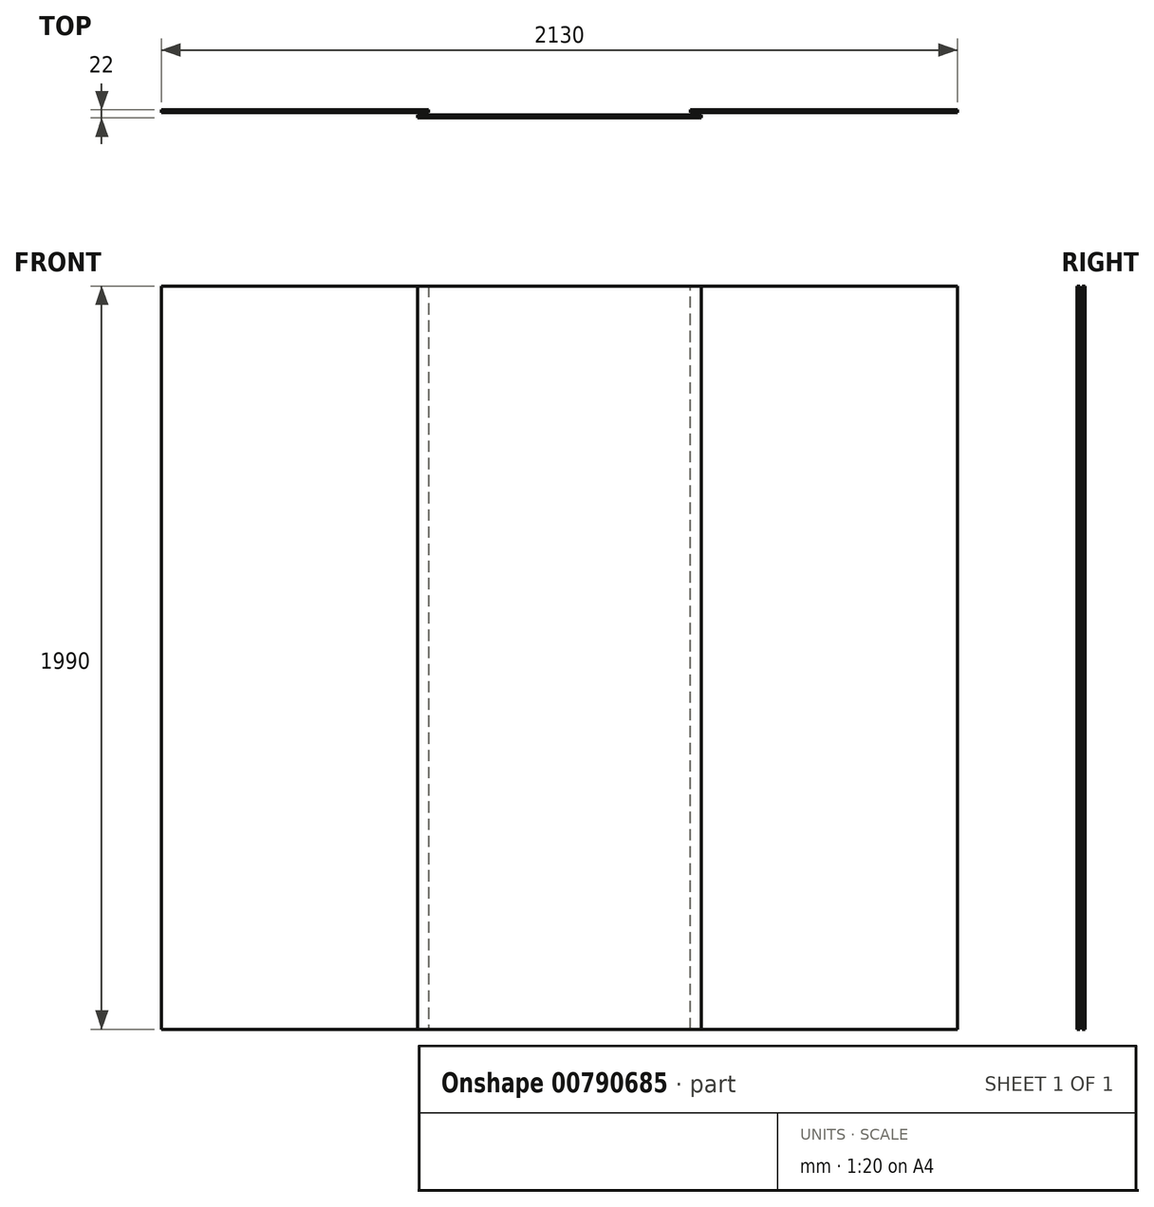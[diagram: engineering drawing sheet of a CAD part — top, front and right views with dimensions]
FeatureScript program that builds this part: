
annotation { "Feature Type Name" : "Feature", "Feature Type Description" : "" }
export const myFeature = defineFeature(function(context is Context, id is Id, definition is map)
    precondition{}
    {
        {
            var Q0;
            Q0=qCreatedBy(makeId("Front.planeOp"),FACE);
            var sketch = newSketch(context, id + "F0", { "sketchPlane" : qUnion([Q0])});
            skLineSegment(sketch, "E0.bottom", {"start": v(0, 0) * mm, "end": v(2140, 0) * mm});
            skLineSegment(sketch, "E0.top", {"start": v(0, 2000) * mm, "end": v(2140, 2000) * mm});
            skLineSegment(sketch, "E0.left", {"start": v(0, 0) * mm, "end": v(0, 2000) * mm});
            skLineSegment(sketch, "E0.right", {"start": v(2140, 0) * mm, "end": v(2140, 2000) * mm});
            skLineSegment(sketch, "E1.bottom", {"start": v(5, 1995) * mm, "end": v(2135, 1995) * mm});
            skLineSegment(sketch, "E1.top", {"start": v(5, 5) * mm, "end": v(2135, 5) * mm});
            skLineSegment(sketch, "E1.left", {"start": v(5, 1995) * mm, "end": v(5, 5) * mm});
            skLineSegment(sketch, "E1.right", {"start": v(2135, 1995) * mm, "end": v(2135, 5) * mm});
            skLineSegment(sketch, "E2.bottom", {"start": v(20, 1950) * mm, "end": v(2120, 1950) * mm});
            skLineSegment(sketch, "E2.top", {"start": v(20, 50) * mm, "end": v(2120, 50) * mm});
            skLineSegment(sketch, "E2.left", {"start": v(20, 1950) * mm, "end": v(20, 50) * mm});
            skLineSegment(sketch, "E2.right", {"start": v(2120, 1950) * mm, "end": v(2120, 50) * mm});
            skLineSegment(sketch, "E3", {"start": v(720, 1995) * mm, "end": v(720, 5) * mm});
            skLineSegment(sketch, "E4", {"start": v(1420, 5) * mm, "end": v(1420, 1995) * mm});
            skLineSegment(sketch, "E5", {"start": v(720, 1000) * mm, "end": v(5, 1000) * mm, "construction": true});
            skLineSegment(sketch, "E6", {"start": v(1420, 1000) * mm, "end": v(2135, 1000) * mm, "construction": true});
            skLineSegment(sketch, "E7", {"start": v(690, 1995) * mm, "end": v(690, 5) * mm});
            skLineSegment(sketch, "E8", {"start": v(1450, 5) * mm, "end": v(1450, 1995) * mm});
            skSolve(sketch);
        }
        {
            var Q0;
            {var subQ0=sQuery(id+"F0.wireOp",EDGE,"E2.left");Q0=makeQuery(id+"F0.imprint","IMPRINT",FACE,{"disambiguationData":[TD([[makeQuery(id+"F0.imprint","IMPRINT",EDGE,{"derivedFrom":subQ0}),1.0]])]});}
            var Q1;
            {var subQ0=sQuery(id+"F0.wireOp",EDGE,"E2.right");Q1=makeQuery(id+"F0.imprint","IMPRINT",FACE,{"disambiguationData":[TD([[makeQuery(id+"F0.imprint","IMPRINT",EDGE,{"derivedFrom":subQ0}),-1.0]])]});}
            var Q2;
            {var subQ4=sQuery(id+"F0.wireOp",EDGE,"E1.right");Q2=makeQuery(id+"F0.imprint","IMPRINT",FACE,{"disambiguationData":[TD([[makeQuery(id+"F0.imprint","IMPRINT",EDGE,{"derivedFrom":subQ4}),-1.0]])]});}
            var Q3;
            {var subQ4=sQuery(id+"F0.wireOp",EDGE,"E1.left");Q3=makeQuery(id+"F0.imprint","IMPRINT",FACE,{"disambiguationData":[TD([[makeQuery(id+"F0.imprint","IMPRINT",EDGE,{"derivedFrom":subQ4}),1.0]])]});}
            var Q4;
            {var subQ0=sQuery(id+"F0.wireOp",EDGE,"E3");var subQ1=sQuery(id+"F0.wireOp",EDGE,"E1.bottom");var subQ2=makeQuery(id+"F0.imprint","INTERSECT",VERTEX,{"derivedFrom":[subQ1,subQ0]});Q4=makeQuery(id+"F0.imprint","IMPRINT",FACE,{"disambiguationData":[TD([[makeQuery(id+"F0.imprint","IMPRINT",EDGE,{"disambiguationData":[TD([[subQ2,1.0]])],"derivedFrom":subQ1}),-1.0]])]});}
            var Q5;
            {var subQ0=sQuery(id+"F0.wireOp",EDGE,"E7");var subQ1=sQuery(id+"F0.wireOp",EDGE,"E2.bottom");var subQ2=makeQuery(id+"F0.imprint","INTERSECT",VERTEX,{"derivedFrom":[subQ1,subQ0]});Q5=makeQuery(id+"F0.imprint","IMPRINT",FACE,{"disambiguationData":[TD([[makeQuery(id+"F0.imprint","IMPRINT",EDGE,{"disambiguationData":[TD([[subQ2,-1.0]])],"derivedFrom":subQ1}),-1.0]])]});}
            var Q6;
            {var subQ0=sQuery(id+"F0.wireOp",EDGE,"E4");var subQ1=sQuery(id+"F0.wireOp",EDGE,"E1.bottom");var subQ2=makeQuery(id+"F0.imprint","INTERSECT",VERTEX,{"derivedFrom":[subQ1,subQ0]});Q6=makeQuery(id+"F0.imprint","IMPRINT",FACE,{"disambiguationData":[TD([[makeQuery(id+"F0.imprint","IMPRINT",EDGE,{"disambiguationData":[TD([[subQ2,-1.0]])],"derivedFrom":subQ1}),-1.0]])]});}
            var Q7;
            {var subQ0=sQuery(id+"F0.wireOp",EDGE,"E4");var subQ1=sQuery(id+"F0.wireOp",EDGE,"E2.bottom");var subQ2=makeQuery(id+"F0.imprint","INTERSECT",VERTEX,{"derivedFrom":[subQ1,subQ0]});Q7=makeQuery(id+"F0.imprint","IMPRINT",FACE,{"disambiguationData":[TD([[makeQuery(id+"F0.imprint","IMPRINT",EDGE,{"disambiguationData":[TD([[subQ2,-1.0]])],"derivedFrom":subQ1}),-1.0]])]});}
            var Q8;
            {var subQ0=sQuery(id+"F0.wireOp",EDGE,"E4");var subQ1=sQuery(id+"F0.wireOp",EDGE,"E1.top");var subQ2=makeQuery(id+"F0.imprint","INTERSECT",VERTEX,{"derivedFrom":[subQ1,subQ0]});Q8=makeQuery(id+"F0.imprint","IMPRINT",FACE,{"disambiguationData":[TD([[makeQuery(id+"F0.imprint","IMPRINT",EDGE,{"disambiguationData":[TD([[subQ2,-1.0]])],"derivedFrom":subQ1}),1.0]])]});}
            var Q9;
            {var subQ0=sQuery(id+"F0.wireOp",EDGE,"E3");var subQ1=sQuery(id+"F0.wireOp",EDGE,"E1.top");var subQ2=makeQuery(id+"F0.imprint","INTERSECT",VERTEX,{"derivedFrom":[subQ1,subQ0]});Q9=makeQuery(id+"F0.imprint","IMPRINT",FACE,{"disambiguationData":[TD([[makeQuery(id+"F0.imprint","IMPRINT",EDGE,{"disambiguationData":[TD([[subQ2,1.0]])],"derivedFrom":subQ1}),1.0]])]});}
            extrude(context, id + "F1", {"entities" : qUnion([Q0, Q1, Q2, Q3, Q4, Q5, Q6, Q7, Q8, Q9]), "oppositeDirection" : true, "depth" : 11 * mm, "offsetDistance" : 25 * mm, "hasSecondDirection" : true, "secondDirectionOppositeDirection" : true, "secondDirectionDepth" : 3 * mm});
        }
        {
            var Q0;
            {var subQ0=sQuery(id+"F0.wireOp",EDGE,"E3");var subQ1=sQuery(id+"F0.wireOp",EDGE,"E1.bottom");var subQ2=makeQuery(id+"F0.imprint","INTERSECT",VERTEX,{"derivedFrom":[subQ1,subQ0]});Q0=makeQuery(id+"F0.imprint","IMPRINT",FACE,{"disambiguationData":[TD([[makeQuery(id+"F0.imprint","IMPRINT",EDGE,{"disambiguationData":[TD([[subQ2,-1.0]])],"derivedFrom":subQ1}),-1.0]])]});}
            var Q1;
            {var subQ0=sQuery(id+"F0.wireOp",EDGE,"E3");var subQ1=sQuery(id+"F0.wireOp",EDGE,"E2.bottom");var subQ2=makeQuery(id+"F0.imprint","INTERSECT",VERTEX,{"derivedFrom":[subQ1,subQ0]});Q1=makeQuery(id+"F0.imprint","IMPRINT",FACE,{"disambiguationData":[TD([[makeQuery(id+"F0.imprint","IMPRINT",EDGE,{"disambiguationData":[TD([[subQ2,-1.0]])],"derivedFrom":subQ1}),-1.0]])]});}
            var Q2;
            {var subQ0=sQuery(id+"F0.wireOp",EDGE,"E4");var subQ1=sQuery(id+"F0.wireOp",EDGE,"E1.bottom");var subQ2=makeQuery(id+"F0.imprint","INTERSECT",VERTEX,{"derivedFrom":[subQ1,subQ0]});Q2=makeQuery(id+"F0.imprint","IMPRINT",FACE,{"disambiguationData":[TD([[makeQuery(id+"F0.imprint","IMPRINT",EDGE,{"disambiguationData":[TD([[subQ2,-1.0]])],"derivedFrom":subQ1}),-1.0]])]});}
            var Q3;
            {var subQ0=sQuery(id+"F0.wireOp",EDGE,"E4");var subQ1=sQuery(id+"F0.wireOp",EDGE,"E2.bottom");var subQ2=makeQuery(id+"F0.imprint","INTERSECT",VERTEX,{"derivedFrom":[subQ1,subQ0]});Q3=makeQuery(id+"F0.imprint","IMPRINT",FACE,{"disambiguationData":[TD([[makeQuery(id+"F0.imprint","IMPRINT",EDGE,{"disambiguationData":[TD([[subQ2,-1.0]])],"derivedFrom":subQ1}),-1.0]])]});}
            var Q4;
            {var subQ0=sQuery(id+"F0.wireOp",EDGE,"E3");var subQ1=sQuery(id+"F0.wireOp",EDGE,"E1.bottom");var subQ2=makeQuery(id+"F0.imprint","INTERSECT",VERTEX,{"derivedFrom":[subQ1,subQ0]});Q4=makeQuery(id+"F0.imprint","IMPRINT",FACE,{"disambiguationData":[TD([[makeQuery(id+"F0.imprint","IMPRINT",EDGE,{"disambiguationData":[TD([[subQ2,1.0]])],"derivedFrom":subQ1}),-1.0]])]});}
            var Q5;
            {var subQ0=sQuery(id+"F0.wireOp",EDGE,"E7");var subQ1=sQuery(id+"F0.wireOp",EDGE,"E2.bottom");var subQ2=makeQuery(id+"F0.imprint","INTERSECT",VERTEX,{"derivedFrom":[subQ1,subQ0]});Q5=makeQuery(id+"F0.imprint","IMPRINT",FACE,{"disambiguationData":[TD([[makeQuery(id+"F0.imprint","IMPRINT",EDGE,{"disambiguationData":[TD([[subQ2,-1.0]])],"derivedFrom":subQ1}),-1.0]])]});}
            var Q6;
            {var subQ0=sQuery(id+"F0.wireOp",EDGE,"E3");var subQ1=sQuery(id+"F0.wireOp",EDGE,"E1.top");var subQ2=makeQuery(id+"F0.imprint","INTERSECT",VERTEX,{"derivedFrom":[subQ1,subQ0]});Q6=makeQuery(id+"F0.imprint","IMPRINT",FACE,{"disambiguationData":[TD([[makeQuery(id+"F0.imprint","IMPRINT",EDGE,{"disambiguationData":[TD([[subQ2,1.0]])],"derivedFrom":subQ1}),1.0]])]});}
            var Q7;
            {var subQ0=sQuery(id+"F0.wireOp",EDGE,"E3");var subQ1=sQuery(id+"F0.wireOp",EDGE,"E1.top");var subQ2=makeQuery(id+"F0.imprint","INTERSECT",VERTEX,{"derivedFrom":[subQ1,subQ0]});Q7=makeQuery(id+"F0.imprint","IMPRINT",FACE,{"disambiguationData":[TD([[makeQuery(id+"F0.imprint","IMPRINT",EDGE,{"disambiguationData":[TD([[subQ2,-1.0]])],"derivedFrom":subQ1}),1.0]])]});}
            var Q8;
            {var subQ0=sQuery(id+"F0.wireOp",EDGE,"E4");var subQ1=sQuery(id+"F0.wireOp",EDGE,"E1.top");var subQ2=makeQuery(id+"F0.imprint","INTERSECT",VERTEX,{"derivedFrom":[subQ1,subQ0]});Q8=makeQuery(id+"F0.imprint","IMPRINT",FACE,{"disambiguationData":[TD([[makeQuery(id+"F0.imprint","IMPRINT",EDGE,{"disambiguationData":[TD([[subQ2,-1.0]])],"derivedFrom":subQ1}),1.0]])]});}
            extrude(context, id + "F2", {"entities" : qUnion([Q0, Q1, Q2, Q3, Q4, Q5, Q6, Q7, Q8]), "depth" : 11 * mm, "offsetDistance" : 25 * mm, "hasSecondDirection" : true, "secondDirectionOppositeDirection" : false, "secondDirectionDepth" : 3 * mm});
        }
        {
            var Q0;
            Q0=makeQuery(id+"F2.opExtrude","CAP_FACE",FACE,{"disambiguationData":[OSD([sQuery(id+"F0.wireOp",EDGE,"E1.bottom"),sQuery(id+"F0.wireOp",EDGE,"E1.top"),sQuery(id+"F0.wireOp",EDGE,"E7"),sQuery(id+"F0.wireOp",EDGE,"E8")])],"isStart":false});
            var sketch = newSketch(context, id + "F3", { "sketchPlane" : qUnion([Q0])});
            skLineSegment(sketch, "E9.bottom", {"start": v(750, 1200) * mm, "end": v(770, 1200) * mm});
            skLineSegment(sketch, "E9.top", {"start": v(750, 1180) * mm, "end": v(770, 1180) * mm});
            skLineSegment(sketch, "E9.left", {"start": v(750, 1200) * mm, "end": v(750, 1180) * mm});
            skLineSegment(sketch, "E9.right", {"start": v(770, 1200) * mm, "end": v(770, 1180) * mm});
            skLineSegment(sketch, "E10.bottom", {"start": v(750, 820) * mm, "end": v(770, 820) * mm});
            skLineSegment(sketch, "E10.top", {"start": v(750, 800) * mm, "end": v(770, 800) * mm});
            skLineSegment(sketch, "E10.left", {"start": v(750, 820) * mm, "end": v(750, 800) * mm});
            skLineSegment(sketch, "E10.right", {"start": v(770, 820) * mm, "end": v(770, 800) * mm});
            skLineSegment(sketch, "E11", {"start": v(750, 1180) * mm, "end": v(750, 820) * mm});
            skLineSegment(sketch, "E12", {"start": v(770, 1180) * mm, "end": v(770, 820) * mm});
            skLineSegment(sketch, "E13", {"start": v(750, 1000) * mm, "end": v(750, 0) * mm, "construction": true});
            skLineSegment(sketch, "E14", {"start": v(750, 0) * mm, "end": v(0, 0) * mm, "construction": true});
            skSolve(sketch);
        }
    });
